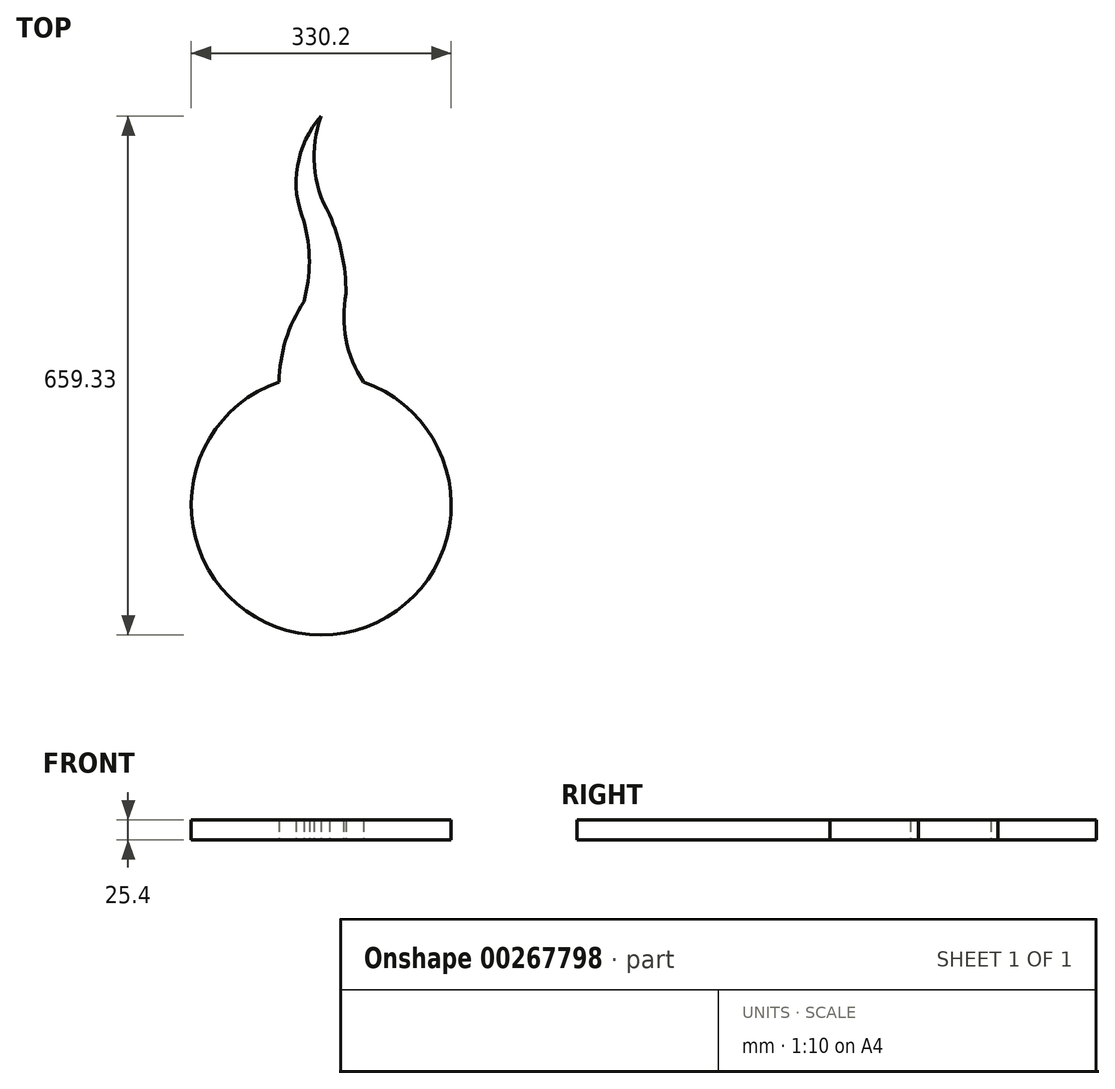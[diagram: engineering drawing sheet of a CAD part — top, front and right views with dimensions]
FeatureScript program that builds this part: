
annotation { "Feature Type Name" : "Feature", "Feature Type Description" : "" }
export const myFeature = defineFeature(function(context is Context, id is Id, definition is map)
    precondition{}
    {
        {
            var Q0;
            Q0=qCreatedBy(makeId("Top.planeOp"),FACE);
            var sketch = newSketch(context, id + "F0", { "sketchPlane" : qUnion([Q0])});
            skArc(sketch, "E0", {"start": v(-53.71, 156.12) * mm, "mid": v(0.02, -165.1) * mm, "end": v(53.67, 156.13) * mm});
            skArc(sketch, "E1", {"start": v(-22, 258.44) * mm, "mid": v(-45.01, 209.5) * mm, "end": v(-53.71, 156.12) * mm});
            skArc(sketch, "E2", {"start": v(-22, 258.44) * mm, "mid": v(-15.06, 309.4) * mm, "end": v(-22, 360.35) * mm});
            skArc(sketch, "E3", {"start": v(0, 494.23) * mm, "mid": v(-30.1, 430.43) * mm, "end": v(-22, 360.35) * mm});
            skPoint(sketch, "E3.startSnap0", {"position": v(0, 389.53) * mm});
            skArc(sketch, "E4", {"start": v(31.63, 268.65) * mm, "mid": v(31.52, 210.2) * mm, "end": v(53.67, 156.13) * mm});
            skArc(sketch, "E5", {"start": v(31.63, 268.65) * mm, "mid": v(26.13, 319.96) * mm, "end": v(10.35, 369.1) * mm});
            skArc(sketch, "E6", {"start": v(0, 494.23) * mm, "mid": v(-8.7, 430.52) * mm, "end": v(10.35, 369.1) * mm});
            skSolve(sketch);
        }
        {
            var Q0;
            Q0 = qSketchRegion(id + "F0", true);
            extrude(context, id + "F1", {"entities" : qUnion([Q0]), "depth" : 25.4 * mm});
        }
    });
